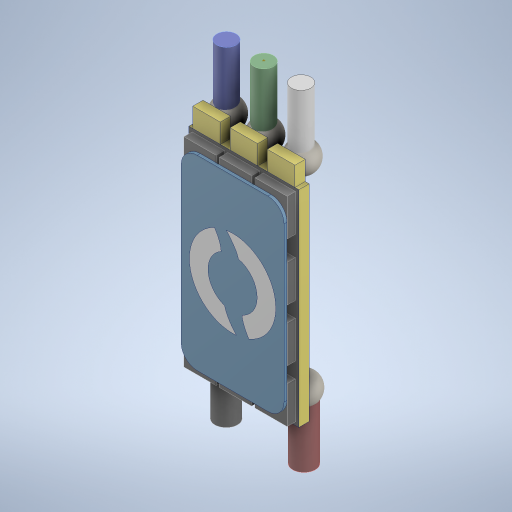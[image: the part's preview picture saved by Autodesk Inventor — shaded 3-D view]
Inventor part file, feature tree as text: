
AUTODESK INVENTOR PART (.ipt)
format: ipt  version: 2024 (Build 280153000, 153)  size: 576,000 bytes
history: native  units: in
note: dims shown in document units (in); Inventor stores cm internally (conversion verified against a paired STEP export)
features: other x24, sketch x3
ambient origin geometry x8: Origin, YZ Plane, XZ Plane, XY Plane, X Axis, Y Axis, Z Axis, Center Point
bodies: Solid1 (feature_tree), Solid2 (feature_tree), Solid3 (feature_tree), Solid4 (feature_tree), Solid5 (feature_tree), Solid6 (feature_tree), Solid7 (feature_tree), Solid8 (feature_tree), Solid9 (feature_tree), Solid10 (feature_tree), Solid11 (feature_tree), Solid12 (feature_tree), Solid13 (feature_tree), Solid14 (feature_tree), Solid15 (feature_tree), Solid16 (feature_tree), Solid17 (feature_tree), Solid18 (feature_tree), Solid19 (feature_tree), Solid20 (feature_tree), Solid21 (feature_tree), Solid22 (feature_tree), Solid23 (feature_tree), Solid24 (feature_tree)
feature tree (27):
  sketch  "Sketch1"
  sketch  "Sketch2"
  sketch  "Sketch3"
  other  "BASICESC-G-PCB-X1-1-solid1"
  other  "BASICESC-E-MOSFET-1-solid1"
  other  "BASICESC-E-MOSFET-2-solid1"
  other  "BASICESC-E-MOSFET-3-solid1"
  other  "BASICESC-E-MOSFET-4-solid1"
  other  "BASICESC-E-MOSFET-5-solid1"
  other  "BASICESC-E-MOSFET-6-solid1"
  other  "BASICESC-E-MOSFET-7-solid1"
  other  "BASICESC-E-MOSFET-8-solid1"
  other  "BASICESC-E-MOSFET-9-solid1"
  other  "BASICESC-E-MOSFET-10-solid1"
  other  "BASICESC-E-MOSFET-11-solid1"
  other  "BASICESC-E-MOSFET-12-solid1"
  other  "BASICESC-M-HEAT-SPREADER-X1-1-solid1"
  other  "Solder Bead-1-solid1"
  other  "Solder Bead-2-solid1"
  other  "Solder Bead-3-solid1"
  other  "Solder Bead-4-solid1"
  other  "Solder Bead-5-solid1"
  other  "14AWG Wire-1-solid1"
  other  "14AWG Wire-2-solid1"
  other  "16AWG Wire-1-solid1"
  other  "16AWG Wire-2-solid1"
  other  "16AWG Wire-3-solid1"
